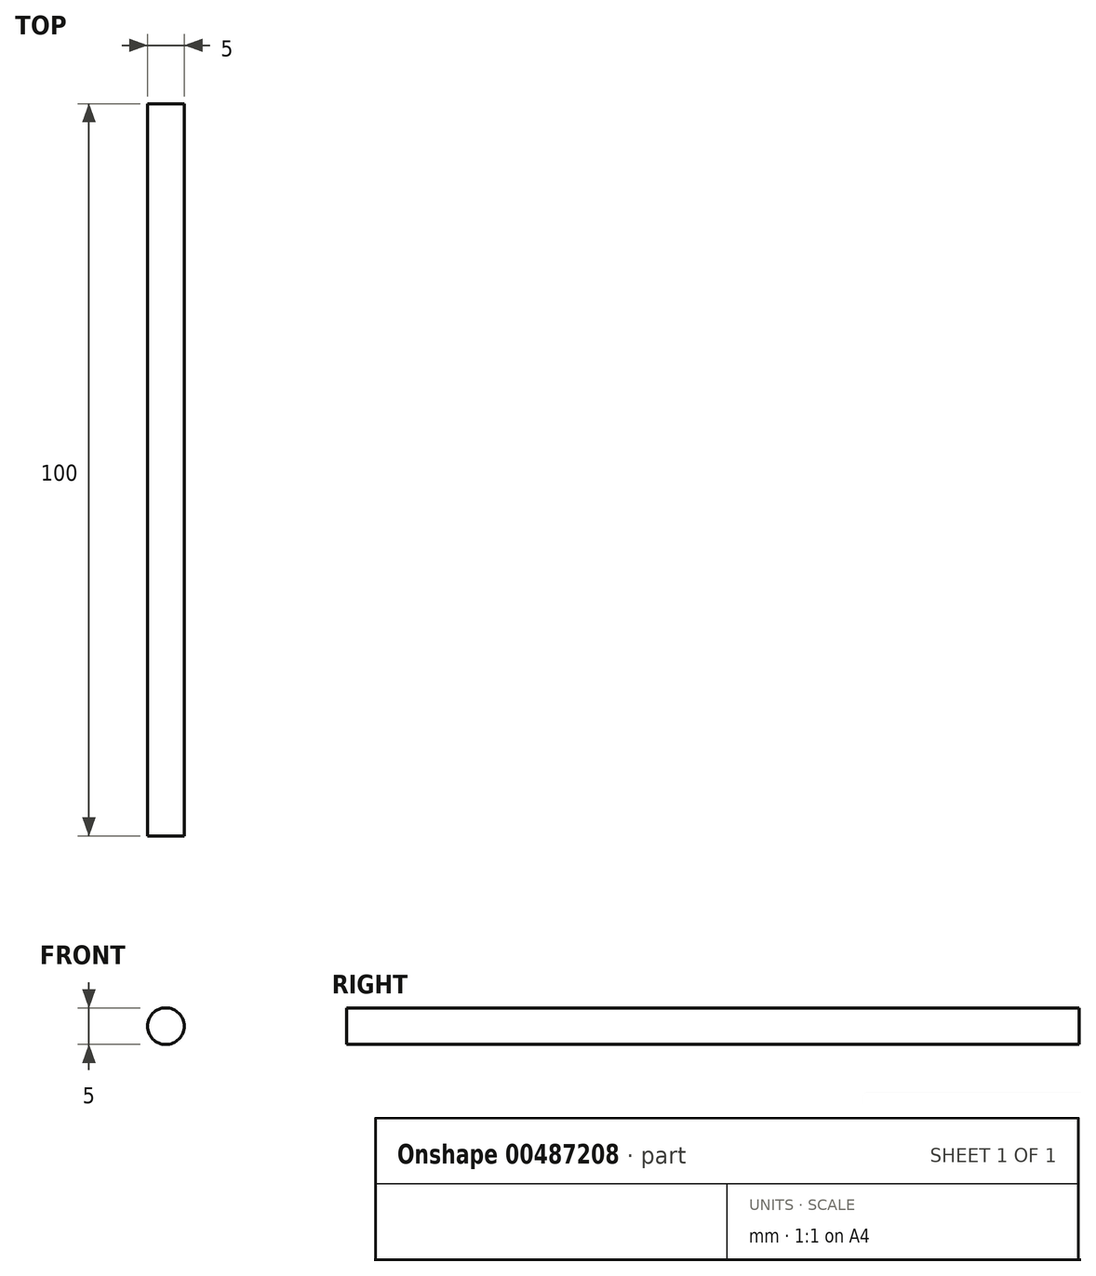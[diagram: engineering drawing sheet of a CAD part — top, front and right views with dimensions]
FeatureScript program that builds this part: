
annotation { "Feature Type Name" : "Feature", "Feature Type Description" : "" }
export const myFeature = defineFeature(function(context is Context, id is Id, definition is map)
    precondition{}
    {
        {
            var Q0;
            Q0=qCreatedBy(makeId("Front.planeOp"),FACE);
            var sketch = newSketch(context, id + "F0", { "sketchPlane" : qUnion([Q0])});
            skCircle(sketch, "E0", {"center": v(0, 0) * mm, "radius": 2.5 * mm});
            skSolve(sketch);
        }
        {
            var Q0;
            Q0 = qSketchRegion(id + "F0", true);
            extrude(context, id + "F1", {"entities" : qUnion([Q0]), "depth" : 100 * mm});
        }
    });
